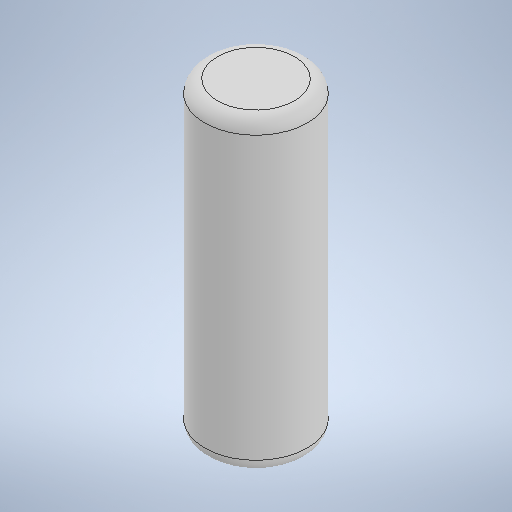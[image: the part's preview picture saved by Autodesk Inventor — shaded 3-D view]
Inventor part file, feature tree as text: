
AUTODESK INVENTOR PART (.ipt)
format: ipt  version: 2025.1 (Build 291241000, 241)  size: 239,616 bytes
history: native  units: mm
features: extrude x1, fillet x1, sketch x1
ambient origin geometry x8: Origin, YZ Plane, XZ Plane, XY Plane, X Axis, Y Axis, Z Axis, Center Point
bodies: Solid1 (feature_tree)
feature tree (3):
  extrude  "Extrusion1"  Depth=12.0mm TaperAngle=0.0deg
  fillet  "Fillet1"  Radius=0.5mm
  sketch  "Sketch1"  dims[d0=4.0mm d1=12.0mm d2=0.0mm d3=0.5mm]
